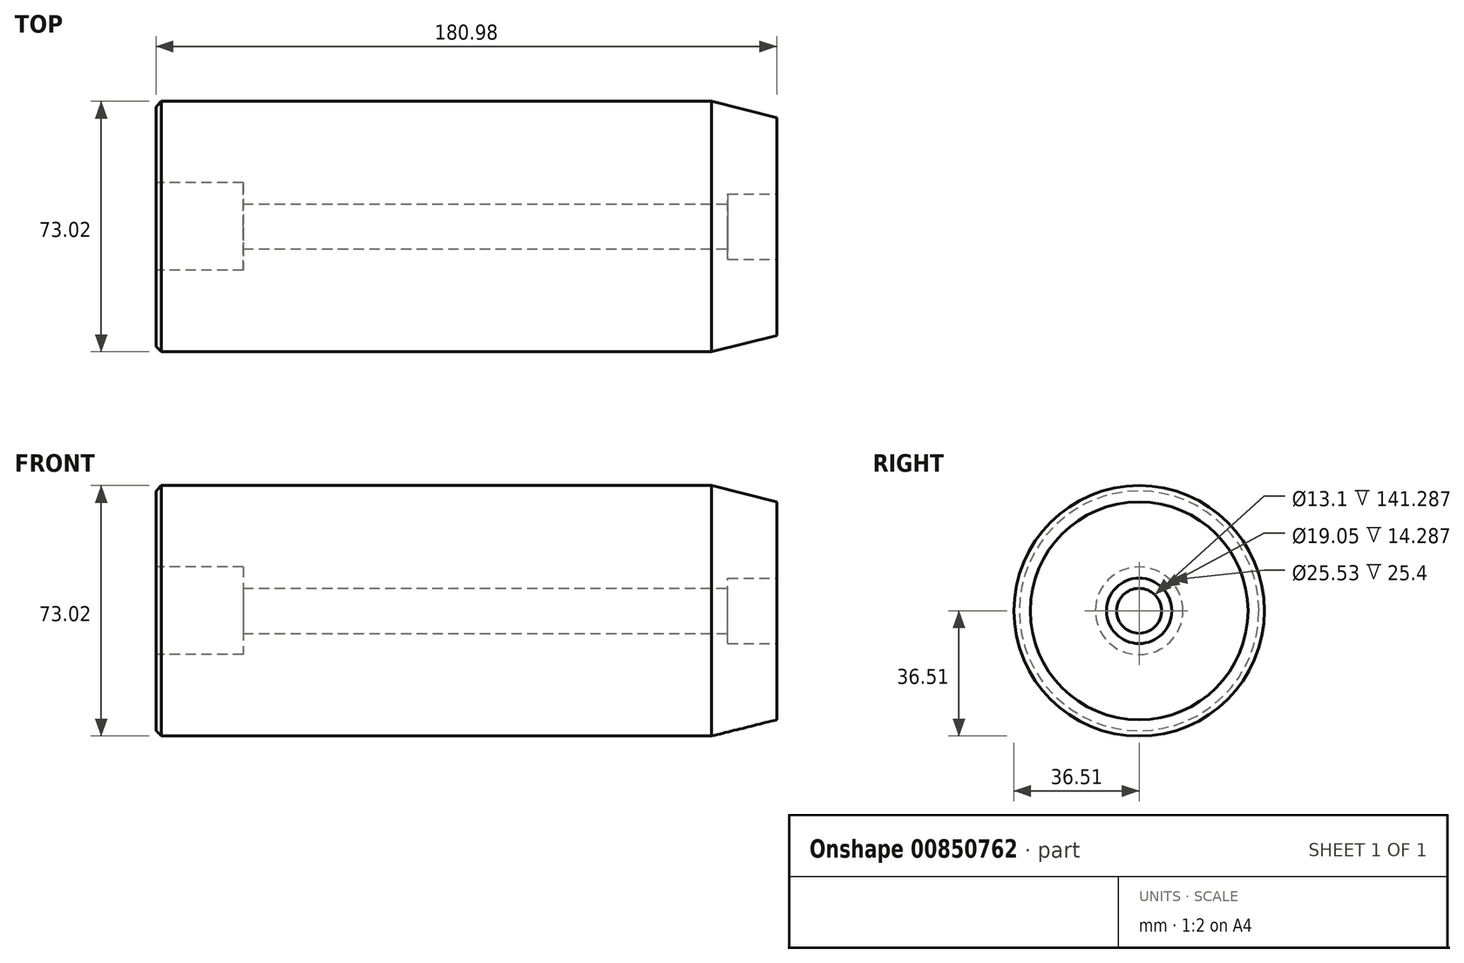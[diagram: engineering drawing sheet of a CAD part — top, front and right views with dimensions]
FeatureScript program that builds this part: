
annotation { "Feature Type Name" : "Feature", "Feature Type Description" : "" }
export const myFeature = defineFeature(function(context is Context, id is Id, definition is map)
    precondition{}
    {
        {
            var Q0;
            Q0=qCreatedBy(makeId("Right.planeOp"),FACE);
            var sketch = newSketch(context, id + "F0", { "sketchPlane" : qUnion([Q0])});
            skCircle(sketch, "E0", {"center": v(0, 0) * mm, "radius": 36.51 * mm});
            skSolve(sketch);
        }
        {
            var Q0;
            Q0 = qSketchRegion(id + "F0", true);
            extrude(context, id + "F1", {"entities" : qUnion([Q0]), "oppositeDirection" : true, "depth" : 180.97 * mm, "offsetDistance" : 25 * mm});
        }
        {
            var Q0;
            Q0=makeQuery(id+"F1.opExtrude","CAP_FACE",FACE,{"disambiguationData":[OSD([sQuery(id+"F0.wireOp",EDGE,"E0")])],"isStart":true});
            var sketch = newSketch(context, id + "F2", { "sketchPlane" : qUnion([Q0])});
            skCircle(sketch, "E1", {"center": v(0, 0) * mm, "radius": 6.55 * mm});
            skSolve(sketch);
        }
        {
            var Q0;
            Q0 = qSketchRegion(id + "F2", true);
            extrude(context, id + "F3", {"entities" : qUnion([Q0]), "operationType" : NewBodyOperationType.REMOVE, "endBound" : BoundingType.THROUGH_ALL, "oppositeDirection" : true, "depth" : 25 * mm, "offsetDistance" : 25 * mm});
        }
        {
            var Q0;
            Q0=makeQuery(id+"F1.opExtrude","CAP_FACE",FACE,{"disambiguationData":[OSD([sQuery(id+"F0.wireOp",EDGE,"E0")])],"isStart":true});
            var sketch = newSketch(context, id + "F4", { "sketchPlane" : qUnion([Q0])});
            skCircle(sketch, "E2", {"center": v(0, 0) * mm, "radius": 9.53 * mm});
            skSolve(sketch);
        }
        {
            var Q0;
            Q0 = qSketchRegion(id + "F4", true);
            extrude(context, id + "F5", {"entities" : qUnion([Q0]), "operationType" : NewBodyOperationType.REMOVE, "oppositeDirection" : true, "depth" : 14.29 * mm, "offsetDistance" : 25 * mm});
        }
        {
            var Q0;
            Q0=makeQuery(id+"F1.opExtrude","CAP_FACE",FACE,{"disambiguationData":[OSD([sQuery(id+"F0.wireOp",EDGE,"E0")])],"isStart":false});
            var sketch = newSketch(context, id + "F6", { "sketchPlane" : qUnion([Q0])});
            skCircle(sketch, "E3", {"center": v(0, 0) * mm, "radius": 12.76 * mm});
            skSolve(sketch);
        }
        {
            var Q0;
            Q0 = qSketchRegion(id + "F6", true);
            extrude(context, id + "F7", {"entities" : qUnion([Q0]), "operationType" : NewBodyOperationType.REMOVE, "oppositeDirection" : true, "depth" : 25.4 * mm, "offsetDistance" : 25.4 * mm});
        }
        {
            var Q0;
            Q0=makeQuery(id+"F5.boolean.opBoolean","COPY",EDGE,{"derivedFrom":makeQuery(id+"F5.opExtrude","CAP_EDGE",EDGE,{"disambiguationData":[OSD([sQuery(id+"F4.wireOp",EDGE,"E2")])],"isStart":true})});
            var Q1;
            Q1=makeQuery(id+"F1.opExtrude","CAP_EDGE",EDGE,{"disambiguationData":[OSD([sQuery(id+"F0.wireOp",EDGE,"E0")])],"isStart":false});
            var Q2;
            Q2=makeQuery(id+"F7.boolean.opBoolean","COPY",EDGE,{"derivedFrom":makeQuery(id+"F7.opExtrude","CAP_EDGE",EDGE,{"disambiguationData":[OSD([sQuery(id+"F6.wireOp",EDGE,"E3")])],"isStart":true})});
            chamfer(context, id + "F8", {"entities" : qUnion([Q0, Q1, Q2]), "width" : 1.59 * mm, "tangentPropagation" : true});
        }
        {
            var Q0;
            Q0=makeQuery(id+"F1.opExtrude","CAP_EDGE",EDGE,{"disambiguationData":[OSD([sQuery(id+"F0.wireOp",EDGE,"E0")])],"isStart":true});
            chamfer(context, id + "F9", {"entities" : qUnion([Q0]), "chamferType" : ChamferType.TWO_OFFSETS, "width1" : 4.76 * mm, "oppositeDirection" : false, "width2" : 19.05 * mm, "tangentPropagation" : true});
        }
    });
